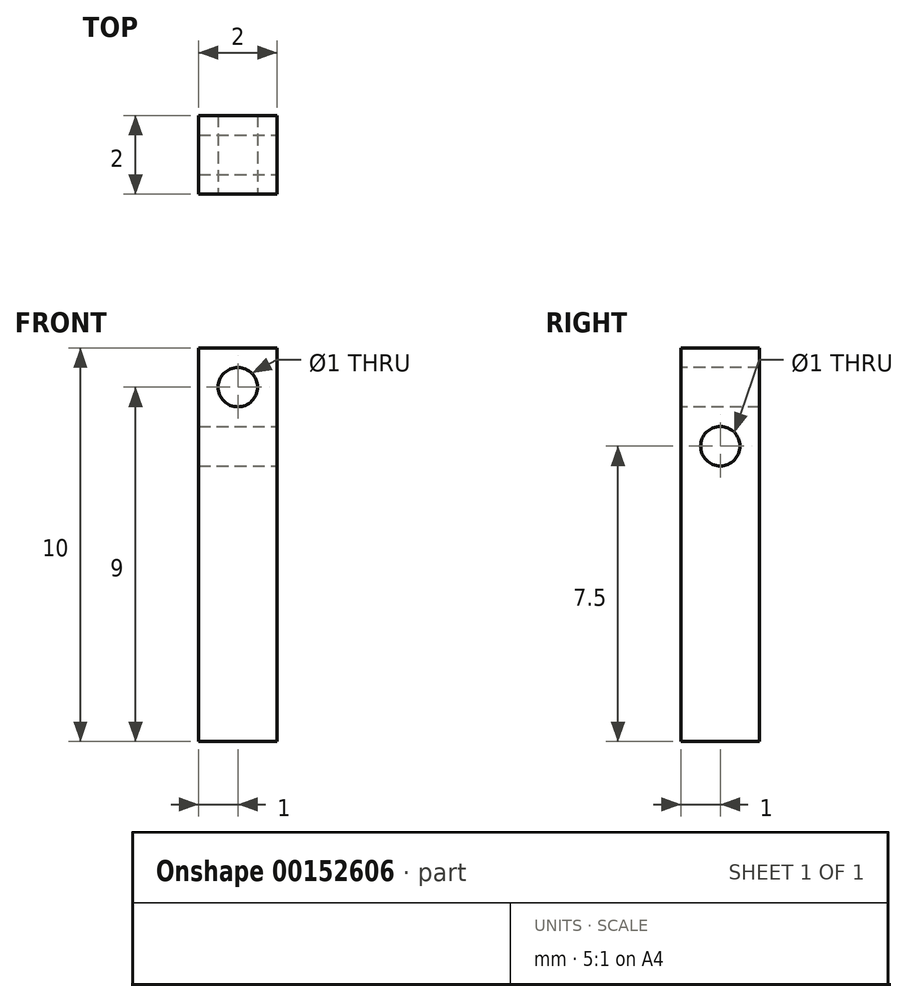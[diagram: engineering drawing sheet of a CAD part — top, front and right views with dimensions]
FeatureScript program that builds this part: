
annotation { "Feature Type Name" : "Feature", "Feature Type Description" : "" }
export const myFeature = defineFeature(function(context is Context, id is Id, definition is map)
    precondition{}
    {
        {
            var Q0;
            Q0=qCreatedBy(makeId("Front.planeOp"),FACE);
            var sketch = newSketch(context, id + "F0", { "sketchPlane" : qUnion([Q0])});
            skLineSegment(sketch, "E0.bottom", {"start": v(-1, 5) * mm, "end": v(1, 5) * mm});
            skLineSegment(sketch, "E0.top", {"start": v(-1, -5) * mm, "end": v(1, -5) * mm});
            skLineSegment(sketch, "E0.left", {"start": v(-1, 5) * mm, "end": v(-1, -5) * mm});
            skLineSegment(sketch, "E0.right", {"start": v(1, 5) * mm, "end": v(1, -5) * mm});
            skPoint(sketch, "E0.middle", {"position": v(0, 0) * mm});
            skSolve(sketch);
        }
        {
            var Q0;
            Q0=makeQuery(id+"F0.imprint","IMPRINT",FACE,{"disambiguationData":[TD([[makeQuery(id+"F0.imprint","IMPRINT",EDGE,{"derivedFrom":sQuery(id+"F0.wireOp",EDGE,"E0.bottom")}),-1.0]])]});
            extrude(context, id + "F1", {"entities" : qUnion([Q0]), "depth" : 2 * mm});
        }
        {
            var Q0;
            Q0=makeQuery(id+"F1.opExtrude","CAP_FACE",FACE,{"disambiguationData":[OSD([sQuery(id+"F0.wireOp",EDGE,"E0.bottom"),sQuery(id+"F0.wireOp",EDGE,"E0.top"),sQuery(id+"F0.wireOp",EDGE,"E0.left"),sQuery(id+"F0.wireOp",EDGE,"E0.right")])],"isStart":false});
            var sketch = newSketch(context, id + "F2", { "sketchPlane" : qUnion([Q0])});
            skPoint(sketch, "E1", {"position": v(0, 4) * mm});
            skPoint(sketch, "E1.positionSnap0", {"position": v(0, 5) * mm});
            skSolve(sketch);
        }
        {
            var Q0;
            Q0=sQuery(id+"F2.wireOp",VERTEX,"E1");
            var Q1;
            Q1=makeQuery(id+"F1.opExtrude","SWEPT_BODY",BODY,{"disambiguationData":[OSD([sQuery(id+"F0.wireOp",EDGE,"E0.bottom"),sQuery(id+"F0.wireOp",EDGE,"E0.top"),sQuery(id+"F0.wireOp",EDGE,"E0.left"),sQuery(id+"F0.wireOp",EDGE,"E0.right")])]});
            hole(context, id + "F3", {"style" : HoleStyle.SIMPLE, "endStyle" : HoleEndStyle.BLIND, "holeDiameter" : 1 * mm, "holeDepth" : 8 * mm, "locations" : qUnion([Q0]), "scope" : qUnion([Q1])});
        }
        {
            var Q0;
            Q0=makeQuery(id+"F1.opExtrude","SWEPT_FACE",FACE,{"disambiguationData":[OSD([sQuery(id+"F0.wireOp",EDGE,"E0.right")])]});
            var sketch = newSketch(context, id + "F4", { "sketchPlane" : qUnion([Q0])});
            skPoint(sketch, "E2", {"position": v(-1, 2.5) * mm});
            skPoint(sketch, "E2.positionSnap0", {"position": v(-1, 5) * mm});
            skSolve(sketch);
        }
        {
            var Q0;
            Q0=sQuery(id+"F4.wireOp",VERTEX,"E2");
            var Q1;
            Q1=makeQuery(id+"F1.opExtrude","SWEPT_BODY",BODY,{"disambiguationData":[OSD([sQuery(id+"F0.wireOp",EDGE,"E0.bottom"),sQuery(id+"F0.wireOp",EDGE,"E0.top"),sQuery(id+"F0.wireOp",EDGE,"E0.left"),sQuery(id+"F0.wireOp",EDGE,"E0.right")])]});
            hole(context, id + "F5", {"style" : HoleStyle.SIMPLE, "endStyle" : HoleEndStyle.BLIND, "holeDiameter" : 1 * mm, "holeDepth" : 8 * mm, "locations" : qUnion([Q0]), "scope" : qUnion([Q1])});
        }
    });
